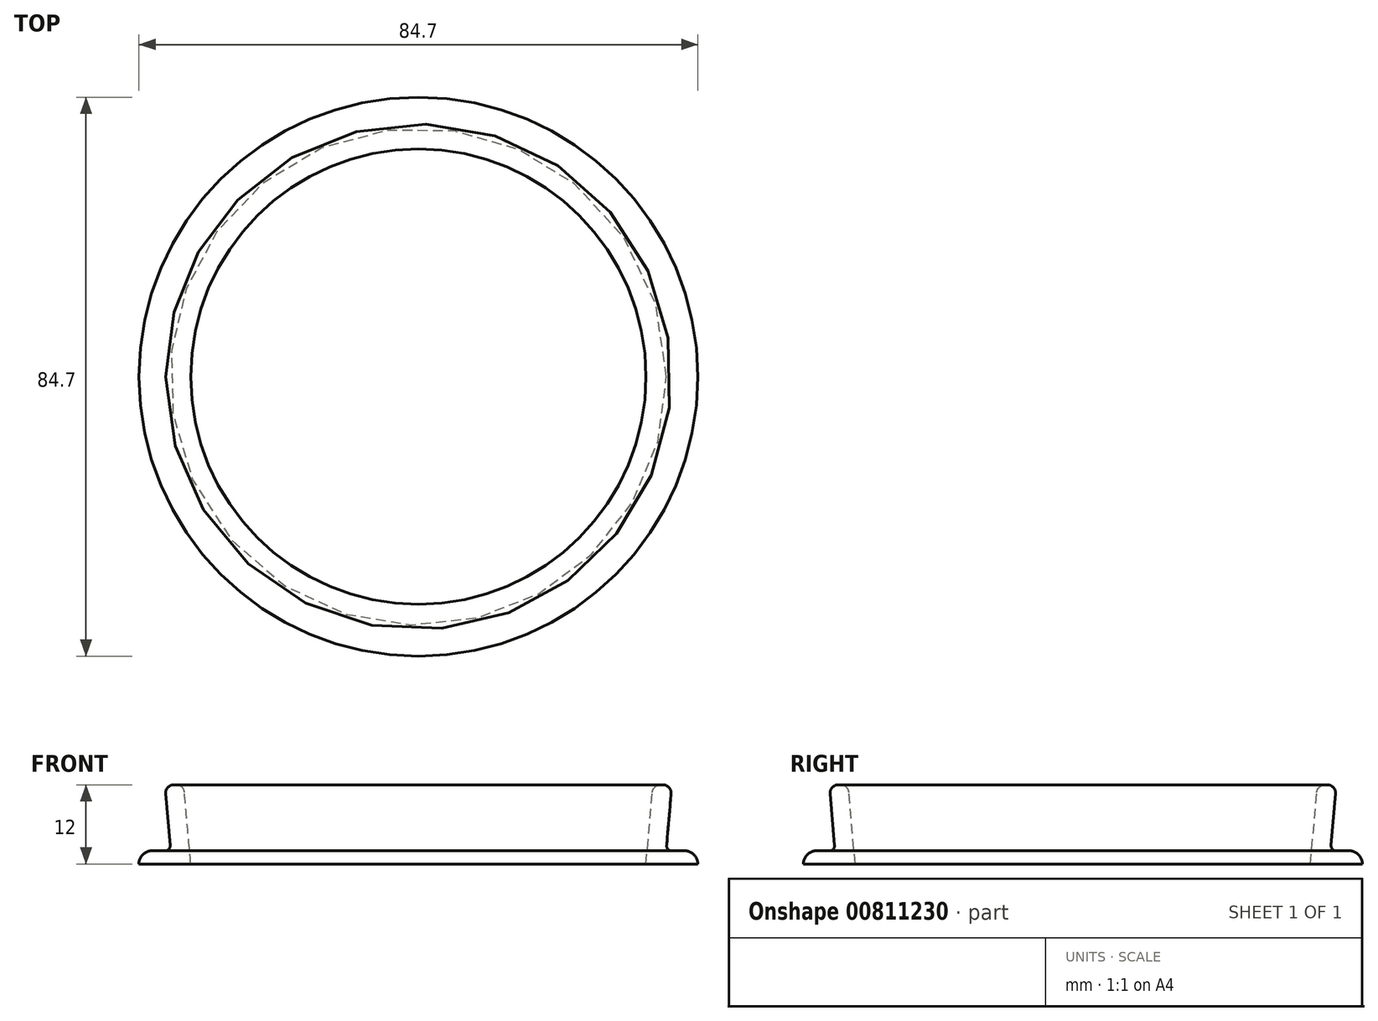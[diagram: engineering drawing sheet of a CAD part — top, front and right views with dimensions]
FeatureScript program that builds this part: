
annotation { "Feature Type Name" : "Feature", "Feature Type Description" : "" }
export const myFeature = defineFeature(function(context is Context, id is Id, definition is map)
    precondition{}
    {
        {
            var Q0;
            Q0=qCreatedBy(makeId("Top.planeOp"),FACE);
            var sketch = newSketch(context, id + "F0", { "sketchPlane" : qUnion([Q0])});
            skCircle(sketch, "E0", {"center": v(0, 0) * mm, "radius": 42 * mm});
            skCircle(sketch, "E1", {"center": v(0, 0) * mm, "radius": 36.5 * mm});
            skSolve(sketch);
        }
        {
            var Q0;
            Q0=qSketchRegion(id+"F0",true);
            extrude(context, id + "F1", {"entities" : qUnion([Q0]), "depth" : 2 * mm, "offsetDistance" : 25 * mm});
        }
        {
            var Q0;
            Q0=qCreatedBy(makeId("Front.planeOp"),FACE);
            var sketch = newSketch(context, id + "F2", { "sketchPlane" : qUnion([Q0])});
            skLineSegment(sketch, "E2", {"start": v(0, 0) * mm, "end": v(0, 127.1) * mm, "construction": true});
            skLineSegment(sketch, "E3.0", {"start": v(-36.5, 0) * mm, "end": v(0, 0) * mm});
            skLineSegment(sketch, "E4.0", {"start": v(-36.5, 2) * mm, "end": v(0, 2) * mm});
            skLineSegment(sketch, "E5", {"start": v(36.5, 2) * mm, "end": v(36.5, 0) * mm});
            skLineSegment(sketch, "E6", {"start": v(34.5, 3) * mm, "end": v(34.5, 14.17) * mm});
            skLineSegment(sketch, "E7", {"start": v(32.5, 2) * mm, "end": v(32.5, 17) * mm});
            skLineSegment(sketch, "E8.trimOffspring", {"start": v(35.5, 2) * mm, "end": v(36.5, 2) * mm});
            skLineSegment(sketch, "E9.trimOffspring", {"start": v(34.5, 0) * mm, "end": v(36.5, 0) * mm});
            skArc(sketch, "E10", {"start": v(35.17, 15.11) * mm, "mid": v(35.65, 18.63) * mm, "end": v(32.5, 17) * mm});
            skPoint(sketch, "E11.visualSharp", {"position": v(34.5, 2) * mm});
            skArc(sketch, "E11.filletArc", {"start": v(34.5, 3) * mm, "mid": v(34.8, 2.3) * mm, "end": v(35.5, 2) * mm});
            skPoint(sketch, "E12.visualSharp", {"position": v(32.5, 0) * mm});
            skArc(sketch, "E12.filletArc", {"start": v(32.5, 2) * mm, "mid": v(33.09, 0.59) * mm, "end": v(34.5, 0) * mm});
            skPoint(sketch, "E13.visualSharp", {"position": v(34.5, 15) * mm});
            skArc(sketch, "E13.filletArc", {"start": v(35.17, 15.11) * mm, "mid": v(34.68, 14.75) * mm, "end": v(34.5, 14.17) * mm});
            skSolve(sketch);
        }
        {
            var Q0;
            Q0=qSketchRegion(id+"F2",true);
            var Q1;
            Q1=sQuery(id+"F2.wireOp",EDGE,"E2");
            revolve(context, id + "F3", {"operationType" : NewBodyOperationType.ADD, "surfaceOperationType" : NewSurfaceOperationType.NEW, "entities" : qUnion([Q0]), "axis" : qUnion([Q1]), "revolveType" : RevolveType.FULL});
        }
        {
            var Q0;
            Q0=makeQuery(id+"F3.boolean.opBoolean","MERGE",FACE,{"derivedFrom":[makeQuery(id+"F1.opExtrude","CAP_FACE",FACE,{"disambiguationData":[OSD([sQuery(id+"F0.wireOp",EDGE,"E0"),sQuery(id+"F0.wireOp",EDGE,"E1")])],"isStart":false}),makeQuery(id+"F3.opRevolve","SWEPT_FACE",FACE,{"disambiguationData":[OSD([sQuery(id+"F2.wireOp",EDGE,"E8.trimOffspring")])]})]});
            var sketch = newSketch(context, id + "F4", { "sketchPlane" : qUnion([Q0])});
            skCircle(sketch, "E14.0", {"center": v(0, 0) * mm, "radius": 42 * mm});
            skCircle(sketch, "E15", {"center": v(0, 0) * mm, "radius": 42.35 * mm});
            skSolve(sketch);
        }
        {
            var Q0;
            Q0=qSketchRegion(id+"F4",true);
            extrude(context, id + "F5", {"entities" : qUnion([Q0]), "operationType" : NewBodyOperationType.ADD, "oppositeDirection" : true, "depth" : 2 * mm, "offsetDistance" : 25 * mm});
        }
        {
            var Q0;
            Q0=makeQuery(id+"F5.opExtrude","CAP_EDGE",EDGE,{"disambiguationData":[OSD([sQuery(id+"F4.wireOp",EDGE,"E15")])],"isStart":true});
            fillet(context, id + "F6", {"entities" : qUnion([Q0]), "radius" : 2 * mm, "tangentPropagation" : true, "allowEdgeOverflow" : false});
        }
        {
            var Q0;
            Q0=makeQuery(id+"F5.boolean.opBoolean","MERGE",FACE,{"derivedFrom":[makeQuery(id+"F3.boolean.opBoolean","MERGE",FACE,{"derivedFrom":[makeQuery(id+"F1.opExtrude","CAP_FACE",FACE,{"disambiguationData":[OSD([sQuery(id+"F0.wireOp",EDGE,"E0"),sQuery(id+"F0.wireOp",EDGE,"E1")])],"isStart":true}),makeQuery(id+"F3.opRevolve","SWEPT_FACE",FACE,{"disambiguationData":[OSD([sQuery(id+"F2.wireOp",EDGE,"E9.trimOffspring")])]})]}),makeQuery(id+"F5.opExtrude","CAP_FACE",FACE,{"disambiguationData":[OSD([sQuery(id+"F4.wireOp",EDGE,"E14.0"),sQuery(id+"F4.wireOp",EDGE,"E15")])],"isStart":false})]});
            var sketch = newSketch(context, id + "F7", { "sketchPlane" : qUnion([Q0])});
            skCircle(sketch, "E16.0", {"center": v(0, 0) * mm, "radius": 34.5 * mm});
            skCircle(sketch, "E17", {"center": v(0, 0) * mm, "radius": 37.38 * mm});
            skSolve(sketch);
        }
        {
            var Q0;
            Q0 = qSketchRegion(id + "F7", true);
            extrude(context, id + "F8", {"entities" : qUnion([Q0]), "operationType" : NewBodyOperationType.ADD, "oppositeDirection" : true, "depth" : 12 * mm, "offsetDistance" : 25 * mm, "hasDraft" : true, "draftAngle" : 5 * degree});
        }
        {
            var Q0;
            Q0=makeQuery(id+"F8.opExtrude","CAP_FACE",FACE,{"disambiguationData":[OSD([sQuery(id+"F7.wireOp",EDGE,"E16.0"),sQuery(id+"F7.wireOp",EDGE,"E17")])],"isStart":false});
            var sketch = newSketch(context, id + "F9", { "sketchPlane" : qUnion([Q0])});
            skCircle(sketch, "E18.0", {"center": v(0, 0) * mm, "radius": 38.42 * mm});
            skSolve(sketch);
        }
        {
            var Q0;
            Q0 = qSketchRegion(id + "F9", true);
            extrude(context, id + "F10", {"entities" : qUnion([Q0]), "operationType" : NewBodyOperationType.REMOVE, "depth" : 25 * mm, "offsetDistance" : 25 * mm});
        }
        {
            var Q0;
            Q0=makeQuery(id+"F5.boolean.opBoolean","MERGE",FACE,{"derivedFrom":[makeQuery(id+"F3.boolean.opBoolean","MERGE",FACE,{"derivedFrom":[makeQuery(id+"F1.opExtrude","CAP_FACE",FACE,{"disambiguationData":[OSD([sQuery(id+"F0.wireOp",EDGE,"E0"),sQuery(id+"F0.wireOp",EDGE,"E1")])],"isStart":true}),makeQuery(id+"F3.opRevolve","SWEPT_FACE",FACE,{"disambiguationData":[OSD([sQuery(id+"F2.wireOp",EDGE,"E9.trimOffspring")])]})]}),makeQuery(id+"F5.opExtrude","CAP_FACE",FACE,{"disambiguationData":[OSD([sQuery(id+"F4.wireOp",EDGE,"E14.0"),sQuery(id+"F4.wireOp",EDGE,"E15")])],"isStart":false})]});
            var sketch = newSketch(context, id + "F11", { "sketchPlane" : qUnion([Q0])});
            skCircle(sketch, "E19.0", {"center": v(0, 0) * mm, "radius": 34.5 * mm});
            skSolve(sketch);
        }
        {
            var Q0;
            Q0 = qSketchRegion(id + "F11", true);
            extrude(context, id + "F12", {"entities" : qUnion([Q0]), "operationType" : NewBodyOperationType.REMOVE, "oppositeDirection" : true, "depth" : 25 * mm, "offsetDistance" : 25 * mm, "hasDraft" : true, "draftAngle" : 5 * degree});
        }
        {
            var Q0;
            Q0=makeQuery(id+"F8.opExtrude","CAP_EDGE",EDGE,{"disambiguationData":[OSD([sQuery(id+"F7.wireOp",EDGE,"E17")])],"isStart":false});
            var Q1;
            Q1=makeQuery(id+"F12.boolean.opBoolean","INTERSECT",EDGE,{"derivedFrom":[makeQuery(id+"F10.boolean.opBoolean","MERGE",FACE,{"derivedFrom":[makeQuery(id+"F8.opExtrude","CAP_FACE",FACE,{"disambiguationData":[OSD([sQuery(id+"F7.wireOp",EDGE,"E16.0"),sQuery(id+"F7.wireOp",EDGE,"E17")])],"isStart":false}),makeQuery(id+"F10.opExtrude","CAP_FACE",FACE,{"disambiguationData":[OSD([sQuery(id+"F9.wireOp",EDGE,"E18.0")])],"isStart":true})]}),makeQuery(id+"F12.opExtrude","SWEPT_FACE",FACE,{"disambiguationData":[OSD([sQuery(id+"F11.wireOp",EDGE,"E19.0")])]})]});
            fillet(context, id + "F13", {"entities" : qUnion([Q0, Q1]), "radius" : 1.25 * mm, "tangentPropagation" : true, "allowEdgeOverflow" : false});
        }
        {
            var Q0;
            Q0=makeQuery(id+"F8.boolean.opBoolean","INTERSECT",EDGE,{"derivedFrom":[makeQuery(id+"F5.boolean.opBoolean","MERGE",FACE,{"derivedFrom":[makeQuery(id+"F3.boolean.opBoolean","MERGE",FACE,{"derivedFrom":[makeQuery(id+"F1.opExtrude","CAP_FACE",FACE,{"disambiguationData":[OSD([sQuery(id+"F0.wireOp",EDGE,"E0"),sQuery(id+"F0.wireOp",EDGE,"E1")])],"isStart":false}),makeQuery(id+"F3.opRevolve","SWEPT_FACE",FACE,{"disambiguationData":[OSD([sQuery(id+"F2.wireOp",EDGE,"E8.trimOffspring")])]})]}),makeQuery(id+"F5.opExtrude","CAP_FACE",FACE,{"disambiguationData":[OSD([sQuery(id+"F4.wireOp",EDGE,"E14.0"),sQuery(id+"F4.wireOp",EDGE,"E15")])],"isStart":true})]}),makeQuery(id+"F8.opExtrude","SWEPT_FACE",FACE,{"disambiguationData":[OSD([sQuery(id+"F7.wireOp",EDGE,"E17")])]})]});
            fillet(context, id + "F14", {"entities" : qUnion([Q0]), "radius" : 0.75 * mm, "tangentPropagation" : true, "allowEdgeOverflow" : false});
        }
    });
